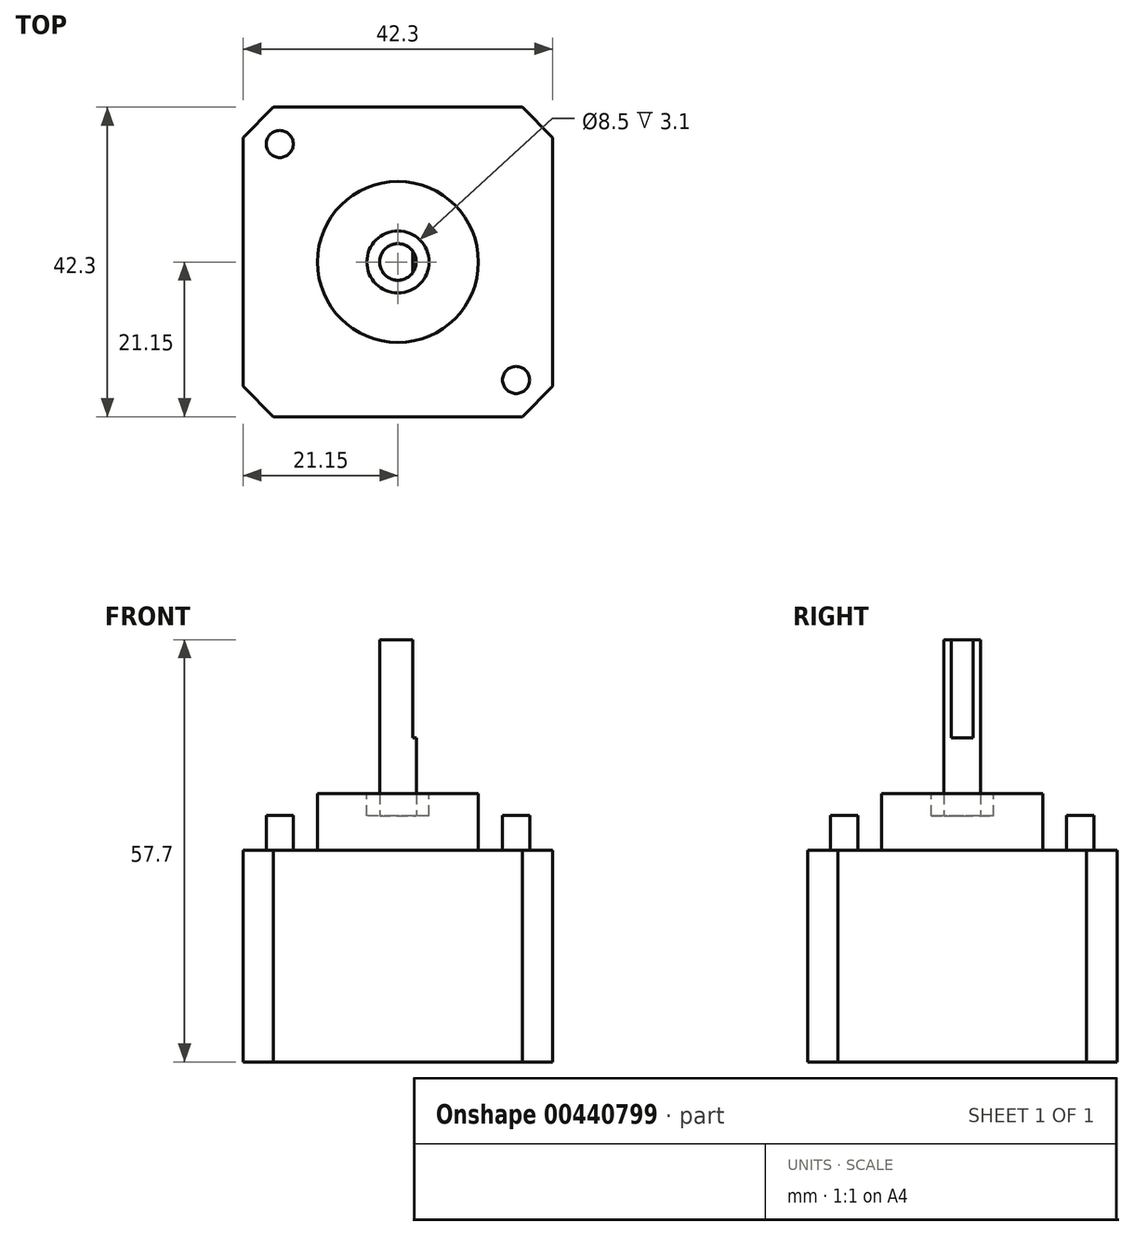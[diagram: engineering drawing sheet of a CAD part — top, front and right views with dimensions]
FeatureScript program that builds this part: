
annotation { "Feature Type Name" : "Feature", "Feature Type Description" : "" }
export const myFeature = defineFeature(function(context is Context, id is Id, definition is map)
    precondition{}
    {
        {
            var Q0;
            Q0=qCreatedBy(makeId("Top.planeOp"),FACE);
            var sketch = newSketch(context, id + "F0", { "sketchPlane" : qUnion([Q0])});
            skPoint(sketch, "E0.middle", {"position": v(0, 0) * mm});
            skLineSegment(sketch, "E1", {"start": v(-21.15, 0) * mm, "end": v(-21.15, -17) * mm});
            skLineSegment(sketch, "E2", {"start": v(0, -21.15) * mm, "end": v(-17, -21.15) * mm});
            skLineSegment(sketch, "E3", {"start": v(-21.15, -17) * mm, "end": v(-17, -21.15) * mm});
            skLineSegment(sketch, "E4.MirrorCS", {"start": v(21.15, 0) * mm, "end": v(21.15, -17) * mm});
            skLineSegment(sketch, "E5.MirrorCS", {"start": v(0, -21.15) * mm, "end": v(17, -21.15) * mm});
            skLineSegment(sketch, "E6.MirrorCS", {"start": v(21.15, -17) * mm, "end": v(17, -21.15) * mm});
            skLineSegment(sketch, "E7.MirrorCS", {"start": v(21.15, 0) * mm, "end": v(21.15, 17) * mm});
            skLineSegment(sketch, "E8.MirrorCS", {"start": v(-21.15, 17) * mm, "end": v(-17, 21.15) * mm});
            skLineSegment(sketch, "E9.MirrorCS", {"start": v(-21.15, 0) * mm, "end": v(-21.15, 17) * mm});
            skLineSegment(sketch, "E10.MirrorCS", {"start": v(0, 21.15) * mm, "end": v(-17, 21.15) * mm});
            skLineSegment(sketch, "E11.MirrorCS", {"start": v(0, 21.15) * mm, "end": v(17, 21.15) * mm});
            skLineSegment(sketch, "E12.MirrorCS", {"start": v(21.15, 17) * mm, "end": v(17, 21.15) * mm});
            skSolve(sketch);
        }
        {
            var Q0;
            Q0=makeQuery(id+"F0.imprint","IMPRINT",FACE,{"disambiguationData":[TD([[makeQuery(id+"F0.imprint","IMPRINT",EDGE,{"derivedFrom":sQuery(id+"F0.wireOp",EDGE,"E1")}),1.0]])]});
            var sketch = newSketch(context, id + "F1", { "sketchPlane" : qUnion([Q0])});
            skLineSegment(sketch, "E13.bottom", {"start": v(8.1, -18.03) * mm, "end": v(-8.1, -18.03) * mm});
            skLineSegment(sketch, "E13.top", {"start": v(8.1, -24.23) * mm, "end": v(-8.1, -24.23) * mm});
            skLineSegment(sketch, "E13.left", {"start": v(8.1, -18.03) * mm, "end": v(8.1, -24.23) * mm});
            skLineSegment(sketch, "E13.right", {"start": v(-8.1, -18.03) * mm, "end": v(-8.1, -24.23) * mm});
            skPoint(sketch, "E13.middle", {"position": v(0, -21.13) * mm});
            skSolve(sketch);
        }
        {
            var Q0;
            {var subQ1=sQuery(id+"F1.wireOp",EDGE,"E13.bottom");Q0=makeQuery(id+"F1.imprint","IMPRINT",FACE,{"disambiguationData":[TD([[makeQuery(id+"F1.imprint","IMPRINT",EDGE,{"derivedFrom":subQ1}),1.0]])]});}
            var Q1;
            {var subQ2=sQuery(id+"F1.wireOp",EDGE,"E13.bottom");Q1=makeQuery(id+"F1.imprint","IMPRINT",FACE,{"disambiguationData":[TD([[makeQuery(id+"F1.imprint","IMPRINT",EDGE,{"derivedFrom":subQ2}),-1.0]])]});}
            extrude(context, id + "F2", {"entities" : qUnion([Q0, Q1]), "depth" : 33.7 * mm});
        }
        {
            var Q0;
            Q0=makeQuery(id+"F2.opExtrude","CAP_FACE",FACE,{"disambiguationData":[OSD([sQuery(id+"F0.wireOp",EDGE,"E1"),sQuery(id+"F0.wireOp",EDGE,"E2"),sQuery(id+"F0.wireOp",EDGE,"E3"),sQuery(id+"F0.wireOp",EDGE,"E4.MirrorCS"),sQuery(id+"F0.wireOp",EDGE,"E5.MirrorCS"),sQuery(id+"F0.wireOp",EDGE,"E6.MirrorCS"),sQuery(id+"F0.wireOp",EDGE,"E7.MirrorCS"),sQuery(id+"F0.wireOp",EDGE,"E8.MirrorCS"),sQuery(id+"F0.wireOp",EDGE,"E9.MirrorCS"),sQuery(id+"F0.wireOp",EDGE,"E10.MirrorCS"),sQuery(id+"F0.wireOp",EDGE,"E11.MirrorCS"),sQuery(id+"F0.wireOp",EDGE,"E12.MirrorCS")])],"isStart":false});
            var sketch = newSketch(context, id + "F3", { "sketchPlane" : qUnion([Q0])});
            skCircle(sketch, "E14", {"center": v(0, 0) * mm, "radius": 11 * mm});
            skSolve(sketch);
        }
        {
            var Q0;
            Q0=makeQuery(id+"F3.imprint","IMPRINT",FACE,{"disambiguationData":[TD([[makeQuery(id+"F3.imprint","IMPRINT",EDGE,{"derivedFrom":sQuery(id+"F3.wireOp",EDGE,"E14")}),1.0]])]});
            extrude(context, id + "F4", {"entities" : qUnion([Q0]), "operationType" : NewBodyOperationType.ADD, "depth" : 3 * mm});
        }
        {
            var Q0;
            Q0=makeQuery(id+"F4.opExtrude","CAP_FACE",FACE,{"disambiguationData":[OSD([sQuery(id+"F3.wireOp",EDGE,"E14")])],"isStart":false});
            var sketch = newSketch(context, id + "F5", { "sketchPlane" : qUnion([Q0])});
            skCircle(sketch, "E15", {"center": v(0, 0) * mm, "radius": 2.5 * mm});
            skCircle(sketch, "E16", {"center": v(0, 0) * mm, "radius": 4.25 * mm});
            skSolve(sketch);
        }
        {
            var Q0;
            Q0 = qSketchRegion(id + "F5", true);
            var Q1;
            Q1=makeQuery(id+"F5.imprint","IMPRINT",FACE,{"disambiguationData":[TD([[makeQuery(id+"F5.imprint","IMPRINT",EDGE,{"derivedFrom":sQuery(id+"F5.wireOp",EDGE,"E15")}),1.0]])]});
            extrude(context, id + "F6", {"entities" : qUnion([Q0, Q1]), "operationType" : NewBodyOperationType.REMOVE, "oppositeDirection" : true, "depth" : 3.1 * mm});
        }
        {
            var Q0;
            Q0=makeQuery(id+"F5.imprint","IMPRINT",FACE,{"disambiguationData":[TD([[makeQuery(id+"F5.imprint","IMPRINT",EDGE,{"derivedFrom":sQuery(id+"F5.wireOp",EDGE,"E15")}),1.0]])]});
            extrude(context, id + "F7", {"entities" : qUnion([Q0]), "operationType" : NewBodyOperationType.ADD, "depth" : 21 * mm, "hasSecondDirection" : true, "secondDirectionOppositeDirection" : true, "secondDirectionDepth" : 25.4 * mm});
        }
        {
            var Q0;
            Q0=makeQuery(id+"F7.opExtrude","CAP_FACE",FACE,{"disambiguationData":[OSD([sQuery(id+"F5.wireOp",EDGE,"E15")])],"isStart":false});
            var sketch = newSketch(context, id + "F8", { "sketchPlane" : qUnion([Q0])});
            skLineSegment(sketch, "E17", {"start": v(-2.5, 0) * mm, "end": v(2, 0) * mm});
            skLineSegment(sketch, "E18", {"start": v(2, 0) * mm, "end": v(2, 1.5) * mm});
            skLineSegment(sketch, "E19", {"start": v(2, 1.5) * mm, "end": v(2, -1.5) * mm});
            skArc(sketch, "E20", {"start": v(0, -2.5) * mm, "mid": v(2.6, 0) * mm, "end": v(0, 2.5) * mm});
            skSolve(sketch);
        }
        {
            var Q0;
            Q0 = qSketchRegion(id + "F8", true);
            var Q1;
            {var subQ0=sQuery(id+"F8.wireOp",EDGE,"E19");var subQ1=makeQuery(id+"F8.imprint","INTERSECT",VERTEX,{"derivedFrom":[sQuery(id+"F8.wireOp",EDGE,"E17"),subQ0]});Q1=makeQuery(id+"F8.imprint","IMPRINT",FACE,{"disambiguationData":[TD([[makeQuery(id+"F8.imprint","IMPRINT",EDGE,{"disambiguationData":[TD([[subQ1,1.0]])],"derivedFrom":subQ0}),1.0]])]});}
            extrude(context, id + "F9", {"entities" : qUnion([Q0, Q1]), "operationType" : NewBodyOperationType.REMOVE, "oppositeDirection" : true, "depth" : 13.4 * mm});
        }
        {
            var Q0;
            Q0=makeQuery(id+"F2.opExtrude","CAP_FACE",FACE,{"disambiguationData":[OSD([sQuery(id+"F0.wireOp",EDGE,"E1"),sQuery(id+"F0.wireOp",EDGE,"E2"),sQuery(id+"F0.wireOp",EDGE,"E3"),sQuery(id+"F0.wireOp",EDGE,"E4.MirrorCS"),sQuery(id+"F0.wireOp",EDGE,"E5.MirrorCS"),sQuery(id+"F0.wireOp",EDGE,"E6.MirrorCS"),sQuery(id+"F0.wireOp",EDGE,"E7.MirrorCS"),sQuery(id+"F0.wireOp",EDGE,"E8.MirrorCS"),sQuery(id+"F0.wireOp",EDGE,"E9.MirrorCS"),sQuery(id+"F0.wireOp",EDGE,"E10.MirrorCS"),sQuery(id+"F0.wireOp",EDGE,"E11.MirrorCS"),sQuery(id+"F0.wireOp",EDGE,"E12.MirrorCS")])],"isStart":false});
            var sketch = newSketch(context, id + "F10", { "sketchPlane" : qUnion([Q0])});
            skCircle(sketch, "E21", {"center": v(-16.15, -16.13) * mm, "radius": 1.85 * mm});
            skCircle(sketch, "E22.MirrorC", {"center": v(16.15, -16.13) * mm, "radius": 1.85 * mm});
            skCircle(sketch, "E23.MirrorC", {"center": v(-16.15, 16.13) * mm, "radius": 1.85 * mm});
            skCircle(sketch, "E24.MirrorC", {"center": v(16.15, 16.13) * mm, "radius": 1.85 * mm});
            skSolve(sketch);
        }
        {
            var Q0;
            Q0=makeQuery(id+"F10.imprint","IMPRINT",FACE,{"disambiguationData":[TD([[makeQuery(id+"F10.imprint","IMPRINT",EDGE,{"derivedFrom":sQuery(id+"F10.wireOp",EDGE,"E23.MirrorC")}),-1.0]])]});
            var Q1;
            Q1=makeQuery(id+"F10.imprint","IMPRINT",FACE,{"disambiguationData":[TD([[makeQuery(id+"F10.imprint","IMPRINT",EDGE,{"derivedFrom":sQuery(id+"F10.wireOp",EDGE,"E24.MirrorC")}),1.0]])]});
            var Q2;
            Q2=makeQuery(id+"F10.imprint","IMPRINT",FACE,{"disambiguationData":[TD([[makeQuery(id+"F10.imprint","IMPRINT",EDGE,{"derivedFrom":sQuery(id+"F10.wireOp",EDGE,"E22.MirrorC")}),-1.0]])]});
            var Q3;
            Q3=makeQuery(id+"F10.imprint","IMPRINT",FACE,{"disambiguationData":[TD([[makeQuery(id+"F10.imprint","IMPRINT",EDGE,{"derivedFrom":sQuery(id+"F10.wireOp",EDGE,"E21")}),1.0]])]});
            extrude(context, id + "F11", {"entities" : qUnion([Q0, Q1, Q2, Q3]), "operationType" : NewBodyOperationType.REMOVE, "oppositeDirection" : true, "depth" : 4.75 * mm});
        }
    });
